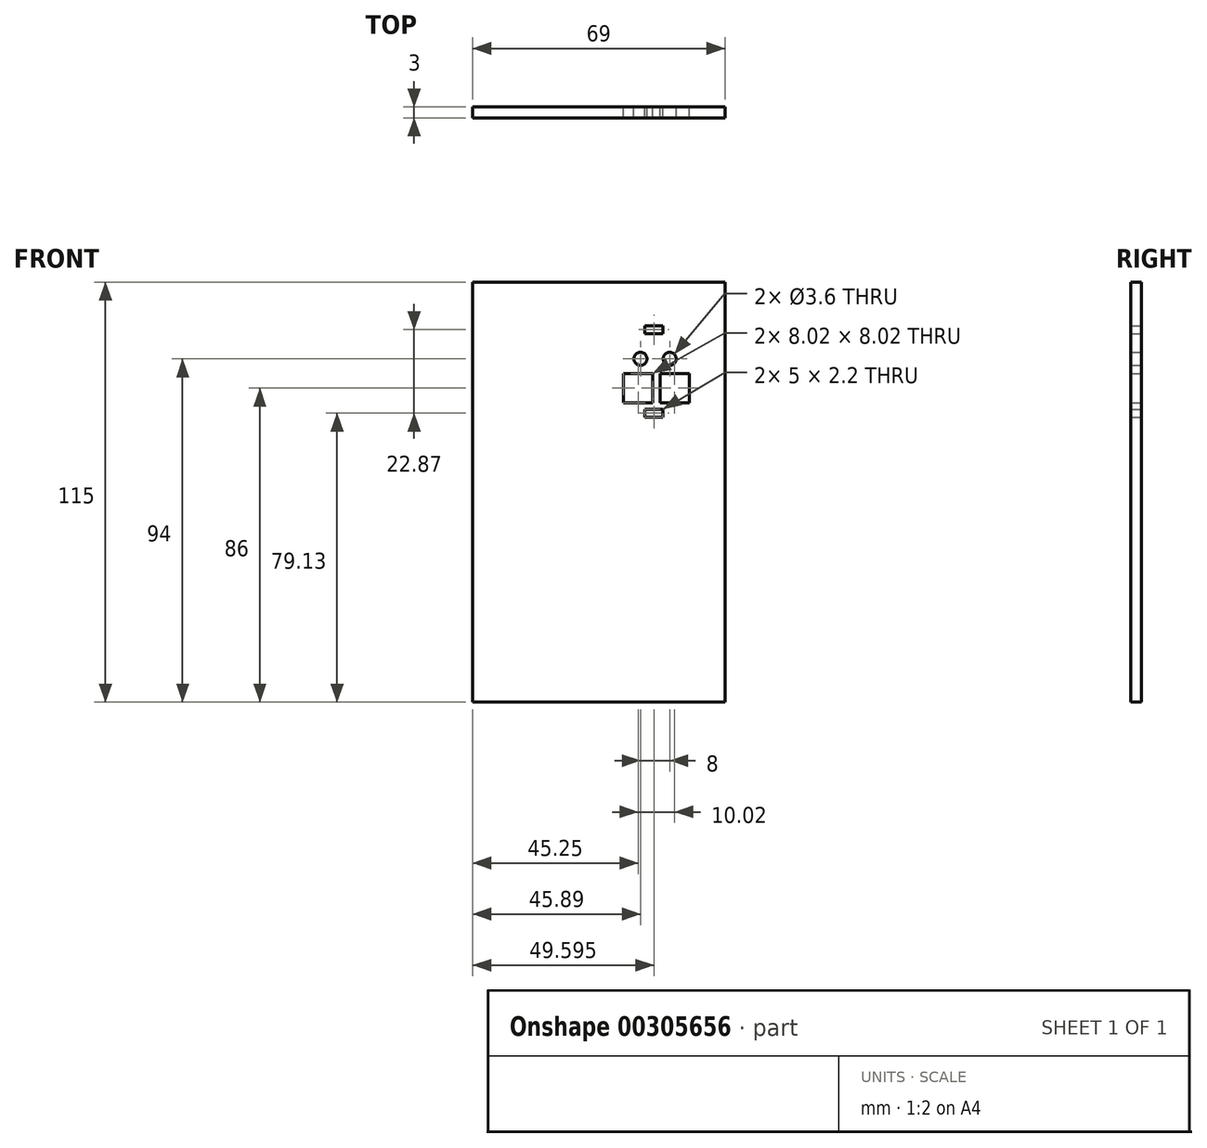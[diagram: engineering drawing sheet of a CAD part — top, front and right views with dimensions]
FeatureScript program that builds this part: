
annotation { "Feature Type Name" : "Feature", "Feature Type Description" : "" }
export const myFeature = defineFeature(function(context is Context, id is Id, definition is map)
    precondition{}
    {
        {
            var Q0;
            Q0=qCreatedBy(makeId("Front.planeOp"),FACE);
            var sketch = newSketch(context, id + "F0", { "sketchPlane" : qUnion([Q0])});
            skLineSegment(sketch, "E0", {"start": v(0, 0) * mm, "end": v(69, 0) * mm});
            skLineSegment(sketch, "E1", {"start": v(69, 0) * mm, "end": v(69, 115) * mm});
            skLineSegment(sketch, "E2", {"start": v(69, 115) * mm, "end": v(0, 115) * mm});
            skLineSegment(sketch, "E3", {"start": v(0, 115) * mm, "end": v(0, 0) * mm});
            skLineSegment(sketch, "E4.0", {"start": v(0, 82.4) * mm, "end": v(69, 82.4) * mm, "construction": true});
            skLineSegment(sketch, "E5.0", {"start": v(58.53, 0) * mm, "end": v(58.53, 115) * mm, "construction": true});
            skLineSegment(sketch, "E6", {"start": v(49.19, 89.6) * mm, "end": v(45.9, 89.6) * mm, "construction": true});
            skLineSegment(sketch, "E7", {"start": v(45.9, 89.6) * mm, "end": v(45.9, 115) * mm, "construction": true});
            skLineSegment(sketch, "E8.0", {"start": v(42, 94) * mm, "end": v(61.67, 94) * mm, "construction": true});
            skCircle(sketch, "E9", {"center": v(45.9, 94) * mm, "radius": 1.8 * mm});
            skLineSegment(sketch, "E10", {"start": v(45.9, 94) * mm, "end": v(53.89, 94) * mm, "construction": true});
            skCircle(sketch, "E11", {"center": v(53.89, 94) * mm, "radius": 1.8 * mm});
            skLineSegment(sketch, "E12.0", {"start": v(68.34, 100.9) * mm, "end": v(45.89, 100.9) * mm, "construction": true});
            skLineSegment(sketch, "E13", {"start": v(58.53, 100.9) * mm, "end": v(58.53, 103.45) * mm});
            skLineSegment(sketch, "E14", {"start": v(52.1, 100.9) * mm, "end": v(52.1, 103.1) * mm});
            skLineSegment(sketch, "E15", {"start": v(52.1, 103.1) * mm, "end": v(47.1, 103.1) * mm});
            skLineSegment(sketch, "E16", {"start": v(47.1, 103.1) * mm, "end": v(47.1, 100.9) * mm});
            skLineSegment(sketch, "E17", {"start": v(47.1, 100.9) * mm, "end": v(52.1, 100.9) * mm});
            skLineSegment(sketch, "E18.0", {"start": v(41.24, 90) * mm, "end": v(49.26, 90) * mm});
            skLineSegment(sketch, "E19.0", {"start": v(49.26, 82) * mm, "end": v(41.24, 82) * mm});
            skLineSegment(sketch, "E20.0", {"start": v(59.28, 82) * mm, "end": v(51.26, 82) * mm});
            skLineSegment(sketch, "E21.0", {"start": v(51.26, 90) * mm, "end": v(59.28, 90) * mm});
            skLineSegment(sketch, "E22.0", {"start": v(59.28, 90) * mm, "end": v(59.28, 82) * mm});
            skLineSegment(sketch, "E23.0", {"start": v(41.24, 90) * mm, "end": v(41.24, 81.99) * mm});
            skLineSegment(sketch, "E24.0", {"start": v(49.26, 90) * mm, "end": v(49.26, 81.99) * mm});
            skLineSegment(sketch, "E25.0", {"start": v(51.26, 82) * mm, "end": v(51.26, 90) * mm});
            skLineSegment(sketch, "E26", {"start": v(47.1, 100.9) * mm, "end": v(47.1, 63.75) * mm, "construction": true});
            skLineSegment(sketch, "E27", {"start": v(52.1, 100.9) * mm, "end": v(52.1, 63.6) * mm, "construction": true});
            skLineSegment(sketch, "E28", {"start": v(52.1, 80.23) * mm, "end": v(52.1, 78.03) * mm});
            skLineSegment(sketch, "E29", {"start": v(52.1, 78.03) * mm, "end": v(47.1, 78.03) * mm});
            skLineSegment(sketch, "E30", {"start": v(47.1, 78.03) * mm, "end": v(47.1, 80.23) * mm});
            skLineSegment(sketch, "E31", {"start": v(47.1, 80.23) * mm, "end": v(52.1, 80.23) * mm});
            skLineSegment(sketch, "E32", {"start": v(52.1, 100.9) * mm, "end": v(49.6, 100.9) * mm, "construction": true});
            skLineSegment(sketch, "E33", {"start": v(49.6, 100.9) * mm, "end": v(49.6, 76.73) * mm, "construction": true});
            skPoint(sketch, "E33.endSnap0", {"position": v(49.6, 78.03) * mm});
            skSolve(sketch);
        }
        {
            var Q0;
            Q0=makeQuery(id+"F0.imprint","IMPRINT",FACE,{"disambiguationData":[TD([[makeQuery(id+"F0.imprint","IMPRINT",EDGE,{"derivedFrom":sQuery(id+"F0.wireOp",EDGE,"E0")}),1.0]])]});
            extrude(context, id + "F1", {"entities" : qUnion([Q0]), "depth" : 3 * mm});
        }
    });
